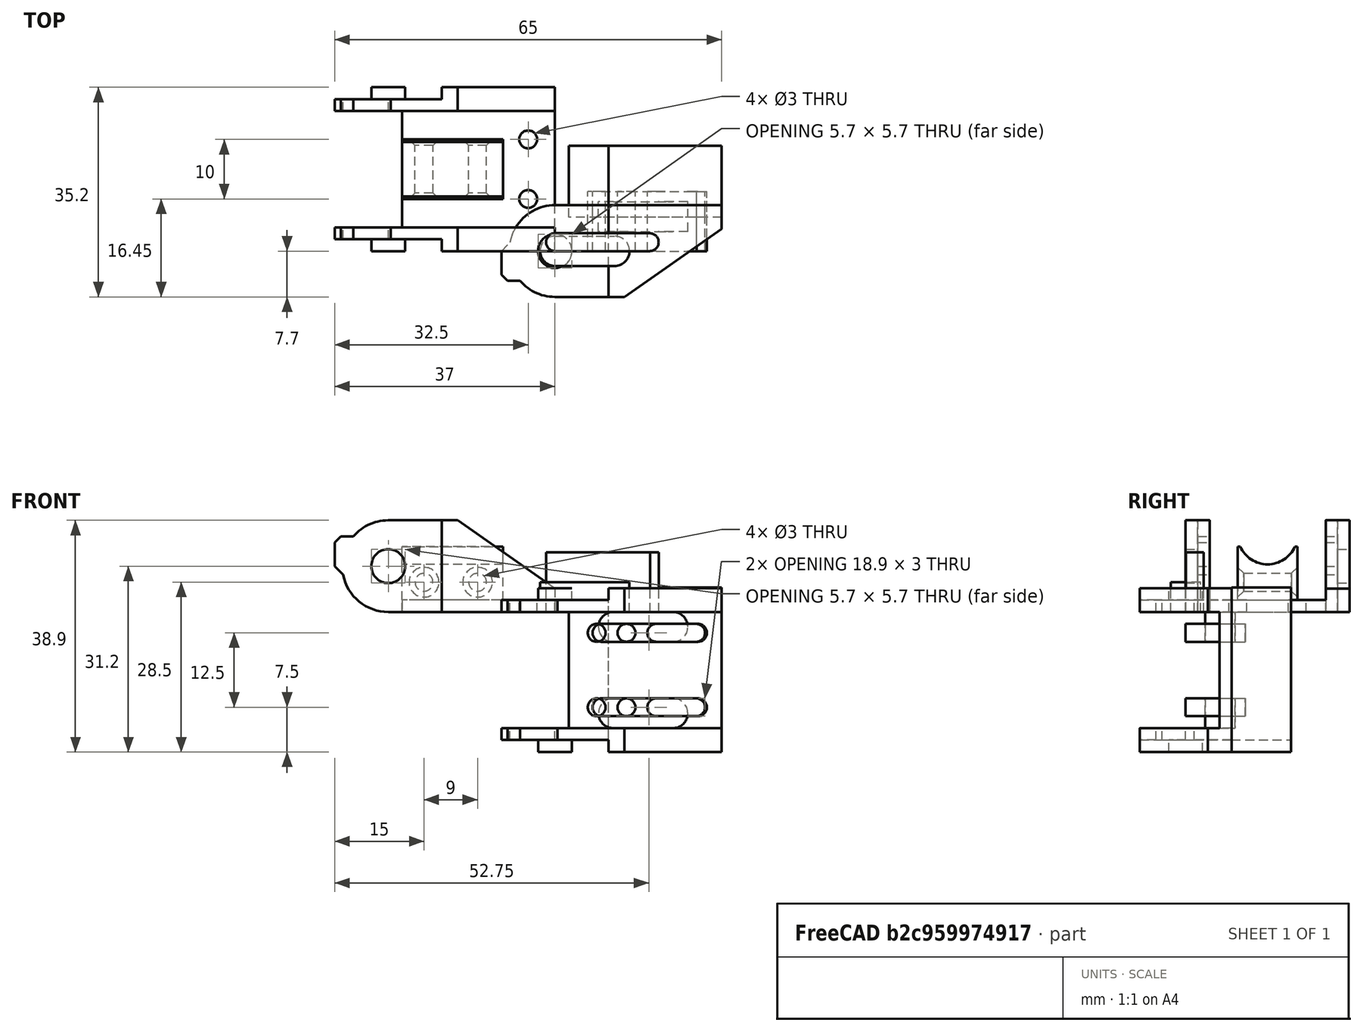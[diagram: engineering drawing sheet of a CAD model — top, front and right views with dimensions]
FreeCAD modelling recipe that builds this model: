
FCSTD DOCUMENT  (FreeCAD 0.18R14555 (Git shallow))
Label: bed-dragchain-top-end
License: All rights reserved
LicenseURL: http://en.wikipedia.org/wiki/All_rights_reserved
objects: Part::Cylinder×17, Part::Box×13, Part::MultiFuse×13, Part::Feature×10, Part::Cut×5, Part::Chamfer×1
note: 59 computed .brp shape members not serialized (recipe doc carries the construction recipe); baked Part::Feature solids carry a one-line shape summary decoded from their .brp

FEATURE [Part::Box] Box001  label="Cube001"
  AttacherType = Attacher::AttachEngine3D
  Height = 2
  Length = 28
  Placement = pos=(0,-7.69,0) rot=(0,0,1;0rad)
  Width = 15.4
FEATURE [Part::Feature] Chamfer_solid  label="right"
  Placement = pos=(0,0,-23) rot=(0,0,1;0rad)
  shape: bbox 37 x 15.41 x 6 mm, 37 faces (baked)
FEATURE [Part::Feature] Fusion001_solid  label="left"
  shape: bbox 37 x 15.41 x 4 mm, 41 faces (baked)
FEATURE [Part::Box] Box005  label="top"
  AttacherType = Attacher::AttachEngine3D
  Height = 23.5
  Length = 25.7
  Placement = pos=(2.3,5.71,-21.5) rot=(0,0,1;0rad)
  Width = 2
FEATURE [Part::Box] Box006  label="Cube005"
  AttacherType = Attacher::AttachEngine3D
  Height = 56
  Length = 38
  Placement = pos=(13.9194,-24.4292,-42) rot=(0,0,1;0.610865rad)
  Width = 15
FEATURE [Part::Box] Box007  label="Cube006"
  AttacherType = Attacher::AttachEngine3D
  Height = 10
  Length = 10
  Placement = pos=(-4,-4,-33.5) rot=(0,0,1;0rad)
  Width = 10
FEATURE [Part::Box] Box008  label="Cube007"
  AttacherType = Attacher::AttachEngine3D
  Height = 2
  Length = 28
  Placement = pos=(0,-7.69,-23) rot=(0,0,1;0rad)
  Width = 15.4
FEATURE [Part::MultiFuse] Fusion  label="left-fixed"
  Shapes = -> [Fusion001_solid,Box001]
FEATURE [Part::MultiFuse] Fusion001  label="right-fixed"
  Placement = pos=(0,0,1.5) rot=(0,0,1;0rad)
  Shapes = -> [Chamfer_solid,Box008]
FEATURE [Part::MultiFuse] Fusion002
  Shapes = -> [Fusion001,Fusion,Box005]
FEATURE [Part::Cut] Cut
  Base = -> Fusion002
  Tool = -> Box007
FEATURE [Part::Cut] Cut001  label="mounter-wo-hole"
  Base = -> Cut
  Placement = pos=(-28,23.5,7.7) rot=(1,0,0;4.71239rad)
  Tool = -> Box006
FEATURE [Part::Cylinder] Cylinder
  Angle = 360
  AttacherType = Attacher::AttachEngine3D
  Height = 5
  Radius = 2.5
FEATURE [Part::Cylinder] Cylinder001
  Angle = 360
  AttacherType = Attacher::AttachEngine3D
  Height = 5
  Placement = pos=(10,0,0) rot=(0,0,1;0rad)
  Radius = 2.5
FEATURE [Part::Box] Box  label="Cube"
  AttacherType = Attacher::AttachEngine3D
  Height = 5
  Length = 10
  Placement = pos=(0,-2.5,0) rot=(0,0,1;0rad)
  Width = 5
FEATURE [Part::MultiFuse] Fusion003  label="hole-template-d5"
  Shapes = -> [Box,Cylinder,Cylinder001]
FEATURE [Part::Feature] Fusion003_solid  label="hole-d5-1"
  Placement = pos=(9.8,3.3,-2.5) rot=(-1,0,0;1.5708rad)
  shape: bbox 15 x 5 x 5 mm, 15 faces (baked)
FEATURE [Part::Feature] Fusion003_solid001  label="holde-d5-2"
  Placement = pos=(9.8,3.3,-17) rot=(-1,0,0;1.5708rad)
  shape: bbox 15 x 5 x 5 mm, 15 faces (baked)
FEATURE [Part::Cylinder] Cylinder002
  Angle = 360
  AttacherType = Attacher::AttachEngine3D
  Height = 10
  Placement = pos=(0,1.5,0) rot=(0,0,1;0rad)
  Radius = 1.5
FEATURE [Part::Cylinder] Cylinder003
  Angle = 360
  AttacherType = Attacher::AttachEngine3D
  Height = 10
  Placement = pos=(15.9,1.5,0) rot=(0,0,1;0rad)
  Radius = 1.5
FEATURE [Part::Box] Box009  label="Cube008"
  AttacherType = Attacher::AttachEngine3D
  Height = 10
  Length = 16
  Width = 3
FEATURE [Part::MultiFuse] Fusion004  label="hole-template-d3"
  Shapes = -> [Box009,Cylinder003,Cylinder002]
FEATURE [Part::Feature] Fusion004_solid  label="hole-d3-1"
  Placement = pos=(7.8,0,-2) rot=(-1,0,0;1.5708rad)
  shape: bbox 18.9 x 10 x 3 mm, 23 faces (baked)
FEATURE [Part::Feature] Fusion004_solid001  label="hole-d3-2"
  Placement = pos=(7.8,3e-15,-14.5) rot=(-1,0,0;1.5708rad)
  shape: bbox 18.9 x 10 x 3 mm, 23 faces (baked)
FEATURE [Part::Feature] Cut002001  label="Cut003"
  shape: bbox 37 x 15.41 x 27.5 mm, 46 faces (baked)
FEATURE [Part::Feature] Cut002001_solid  label="Cut003 (Solid)"
  shape: bbox 37 x 15.41 x 27.5 mm, 46 faces (baked)
FEATURE [Part::Cylinder] Cylinder004
  Angle = 360
  AttacherType = Attacher::AttachEngine3D
  Height = 10
  Placement = pos=(24,-1e-15,-3.5) rot=(-1,0,0;1.5708rad)
  Radius = 1.5
FEATURE [Part::Cylinder] Cylinder005
  Angle = 360
  AttacherType = Attacher::AttachEngine3D
  Height = 10
  Placement = pos=(24,1.8e-15,-16) rot=(-1,0,0;1.5708rad)
  Radius = 1.5
FEATURE [Part::Cylinder] Cylinder006
  Angle = 360
  AttacherType = Attacher::AttachEngine3D
  Height = 10
  Placement = pos=(19,-1e-15,-3.5) rot=(-1,0,0;1.5708rad)
  Radius = 1.5
FEATURE [Part::Cylinder] Cylinder007
  Angle = 360
  AttacherType = Attacher::AttachEngine3D
  Height = 10
  Placement = pos=(19,1.8e-15,-16) rot=(-1,0,0;1.5708rad)
  Radius = 1.5
FEATURE [Part::Cylinder] Cylinder008
  Angle = 360
  AttacherType = Attacher::AttachEngine3D
  Height = 10
  Placement = pos=(14,-1e-15,-3.5) rot=(-1,0,0;1.5708rad)
  Radius = 1.5
FEATURE [Part::Cylinder] Cylinder009
  Angle = 360
  AttacherType = Attacher::AttachEngine3D
  Height = 10
  Placement = pos=(7,-1e-15,-3.5) rot=(-1,0,0;1.5708rad)
  Radius = 1.5
FEATURE [Part::Cylinder] Cylinder010
  Angle = 360
  AttacherType = Attacher::AttachEngine3D
  Height = 10
  Placement = pos=(14,1.8e-15,-16) rot=(-1,0,0;1.5708rad)
  Radius = 1.5
FEATURE [Part::Cylinder] Cylinder011
  Angle = 360
  AttacherType = Attacher::AttachEngine3D
  Height = 10
  Placement = pos=(7,1.8e-15,-16) rot=(-1,0,0;1.5708rad)
  Radius = 1.5
FEATURE [Part::Box] Box010  label="Cube009"
  AttacherType = Attacher::AttachEngine3D
  Height = 3
  Length = 7
  Placement = pos=(7,0,-5) rot=(0,0,1;0rad)
  Width = 10
FEATURE [Part::Box] Box011  label="Cube010"
  AttacherType = Attacher::AttachEngine3D
  Height = 3
  Length = 7
  Placement = pos=(7,0,-17.5) rot=(0,0,1;0rad)
  Width = 10
FEATURE [Part::MultiFuse] Fusion005
  Placement = pos=(10,0,0) rot=(0,0,1;0rad)
  Shapes = -> [Box011,Cylinder011,Cylinder010]
FEATURE [Part::MultiFuse] Fusion006
  Placement = pos=(10,0,0) rot=(0,0,1;0rad)
  Shapes = -> [Cylinder009,Box010,Cylinder008]
FEATURE [Part::MultiFuse] Fusion007
  Placement = pos=(-12,0,0) rot=(0,0,1;0rad)
  Shapes = -> [Cylinder007,Cylinder005]
FEATURE [Part::MultiFuse] Fusion008
  Placement = pos=(-12,0,0) rot=(0,0,1;0rad)
  Shapes = -> [Cylinder006,Cylinder004]
FEATURE [Part::MultiFuse] Fusion009
  Shapes = -> [Fusion008,Fusion007,Fusion006,Fusion005]
FEATURE [Part::Box] Box012  label="Cube011"
  AttacherType = Attacher::AttachEngine3D
  Height = 23.5
  Length = 6.7
  Placement = pos=(2.3,7.7,-21.5) rot=(0,0,1;0rad)
  Width = 10
FEATURE [Part::Box] Box013  label="Cube012"
  AttacherType = Attacher::AttachEngine3D
  Height = 27.6
  Length = 19
  Placement = pos=(9,7.7,-23.5) rot=(0,0,1;0rad)
  Width = 10
FEATURE [Part::Cylinder] Cylinder012
  Angle = 360
  AttacherType = Attacher::AttachEngine3D
  Height = 10
  Placement = pos=(-4.5,8.75,0) rot=(0,0,1;0rad)
  Radius = 1.5
FEATURE [Part::Cylinder] Cylinder013
  Angle = 360
  AttacherType = Attacher::AttachEngine3D
  Height = 10
  Placement = pos=(-4.5,18.75,0) rot=(0,0,1;0rad)
  Radius = 1.5
FEATURE [Part::Box] Box014  label="Cube013"
  AttacherType = Attacher::AttachEngine3D
  Height = 8
  Length = 17
  Placement = pos=(-25.7,8.75,0) rot=(0,0,1;0rad)
  Width = 10
FEATURE [Part::Cylinder] Cylinder015
  Angle = 360
  AttacherType = Attacher::AttachEngine3D
  Height = 17
  Placement = pos=(-22,4.8,5) rot=(1,0,0;4.71239rad)
  Radius = 1.5
FEATURE [Part::MultiFuse] Fusion011
  Placement = pos=(0,0,-1) rot=(0,0,1;0rad)
  Shapes = -> [Cylinder013,Cylinder012]
FEATURE [Part::Cut] Cut002003
  Base = -> Cut001
  Tool = -> Fusion011
FEATURE [Part::Box] Box015  label="Cube014"
  AttacherType = Attacher::AttachEngine3D
  Height = 3
  Length = 17
  Placement = pos=(-25.7,8.75,8) rot=(0,0,1;0rad)
  Width = 10
FEATURE [Part::Cylinder] Cylinder017
  Angle = 360
  AttacherType = Attacher::AttachEngine3D
  Height = 27
  Placement = pos=(-7,13.75,13) rot=(0,1,0;4.71239rad)
  Radius = 5
FEATURE [Part::Cut] Cut002004
  Base = -> Box015
  Tool = -> Cylinder017
FEATURE [Part::Cylinder] Cylinder018
  Angle = 360
  AttacherType = Attacher::AttachEngine3D
  Height = 17
  Placement = pos=(-13,4.8,5) rot=(-1,0,0;1.5708rad)
  Radius = 1.5
FEATURE [Part::MultiFuse] Fusion012
  Shapes = -> [Cylinder018,Cylinder015]
FEATURE [Part::Cut] Cut002005
  Base = -> Box014
  Tool = -> Fusion012
FEATURE [Part::Chamfer] Chamfer
  Base = -> Cut002005
  Edges = 4 edges r=1: [Edge8,Edge9,Edge14,Edge15]
FEATURE [Part::MultiFuse] Fusion013
  Shapes = -> [Chamfer,Cut002003,Cut002004]
FEATURE [Part::Feature] Fusion013001  label="Fusion014"
  shape: bbox 37 x 27.5 x 15.41 mm, 48 faces (baked)
FEATURE [Part::Feature] Fusion013001_solid  label="Fusion014 (Solid)"
  shape: bbox 37 x 27.5 x 15.41 mm, 48 faces (baked)
